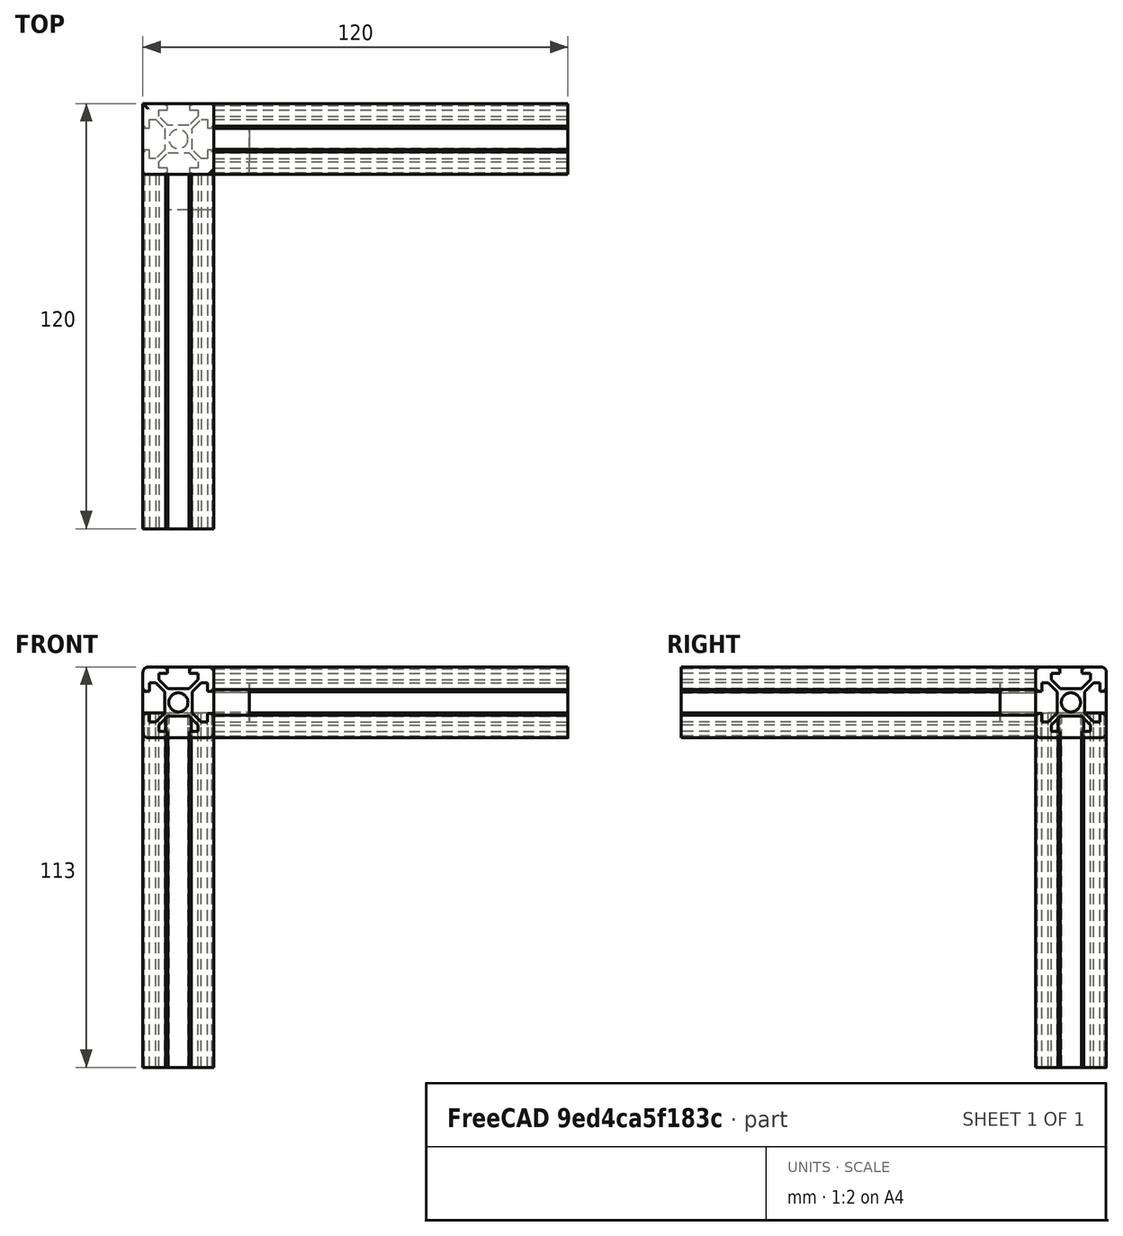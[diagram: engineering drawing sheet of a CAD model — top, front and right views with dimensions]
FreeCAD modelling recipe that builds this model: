
FCSTD DOCUMENT  (FreeCAD 1.0R39109 (Git))
Label: TopHatSpacer_removedinner
License: All rights reserved
LicenseURL: https://en.wikipedia.org/wiki/All_rights_reserved
objects: Part::FeaturePython×17, Part::Cut×8, Part::Feature×6, Part::Cylinder×6, Part::Plane×4, App::DocumentObjectGroup×4, Part::MultiFuse×3, Part::Box×2, PartDesign::FeatureBase×1, PartDesign::Fillet×1, PartDesign::Body×1
note: 52 computed .brp shape members not serialized (recipe doc carries the construction recipe); baked Part::Feature solids carry a one-line shape summary decoded from their .brp

FEATURE [Part::Feature] Part__Feature  label="Extrusion Profiles v3"
  shape: bbox 20 x 20 x 100 mm, 67 faces (baked)
FEATURE [Part::Cylinder] Cylinder
  Angle = 360
  AttacherType = Attacher::AttachEngine3D
  FirstAngle = 0
  Height = 100
  Placement = pos=(10,10,0) rot=(0,0,1;0rad)
  Radius = 2.7
  SecondAngle = 0
FEATURE [Part::Cut] Cut
  Base = -> Part__Feature
  Placement = pos=(0,5.68e-14,93) rot=(1,0,0;1.5708rad)
  Tool = -> Cylinder
FEATURE [Part::Cylinder] Cylinder001
  Angle = 360
  AttacherType = Attacher::AttachEngine3D
  FirstAngle = 0
  Height = 100
  Placement = pos=(10,10,0) rot=(0,0,1;0rad)
  Radius = 2.7
  SecondAngle = 0
FEATURE [Part::Feature] Part__Feature001  label="Extrusion Profiles v004"
  shape: bbox 20 x 20 x 100 mm, 67 faces (baked)
FEATURE [Part::Cut] Cut001
  Base = -> Part__Feature001
  Placement = pos=(20,0,113) rot=(0,1,0;1.5708rad)
  Tool = -> Cylinder001
FEATURE [Part::Cylinder] Cylinder002
  Angle = 360
  AttacherType = Attacher::AttachEngine3D
  FirstAngle = 0
  Height = 100
  Placement = pos=(10,10,0) rot=(0,0,1;0rad)
  Radius = 2.7
  SecondAngle = 0
FEATURE [Part::Feature] Part__Feature002  label="Extrusion Profiles v005"
  shape: bbox 20 x 20 x 100 mm, 67 faces (baked)
FEATURE [Part::Cut] Cut002
  Base = -> Part__Feature002
  Tool = -> Cylinder002
FEATURE [Part::Box] Box  label="Cube"
  AttacherType = Attacher::AttachEngine3D
  Height = 20
  Length = 30
  Placement = pos=(0,-10,93) rot=(0,0,1;0rad)
  Width = 30
FEATURE [Part::MultiFuse] Fusion
  Shapes = -> [Cut,Cut001,Cut002]
FEATURE [Part::Cut] Cut003
  Base = -> Box
  Tool = -> Fusion
FEATURE [Part::Box] Box001  label="Cube001"
  AttacherType = Attacher::AttachEngine3D
  Height = 30
  Length = 10
  Placement = pos=(20,-10,90) rot=(0,0,1;0rad)
  Width = 10
FEATURE [Part::Cut] Cut004
  Base = -> Cut003
  Tool = -> Box001
FEATURE [Part::Plane] Plane
  AttacherType = Attacher::AttachEngine3D
  Length = 100
  Placement = pos=(20,-40,157.445) rot=(0,1,0;1.5708rad)
  Width = 100
FEATURE [Part::FeaturePython] Slice  # WARN: FeaturePython — macro-defined, semantics opaque (R4)
  Base = -> Cut004
  Mode = 1
  Tolerance = 0
  Tools = -> [Plane]
FEATURE [Part::FeaturePython] Slice_child0  label="Slice.0"  # WARN: FeaturePython — macro-defined, semantics opaque (R4)
  Base = -> Slice
  FilterType = 1
  Invert = false
  OverrideMaxVal = 0
  WindowFrom = 80
  WindowTo = 100
  items = 0
FEATURE [App::DocumentObjectGroup] GrExplode_Slice  label="Exploded Slice"
  Group = -> [Slice_child0]
FEATURE [Part::FeaturePython] Slice_child6  label="Slice.6"  # WARN: FeaturePython — macro-defined, semantics opaque (R4)
  Base = -> Slice
  FilterType = 1
  Invert = false
  OverrideMaxVal = 0
  WindowFrom = 80
  WindowTo = 100
  items = 6
FEATURE [Part::FeaturePython] Slice_child8  label="Slice.8"  # WARN: FeaturePython — macro-defined, semantics opaque (R4)
  Base = -> Slice
  FilterType = 1
  Invert = false
  OverrideMaxVal = 0
  WindowFrom = 80
  WindowTo = 100
  items = 8
FEATURE [Part::Plane] Plane001
  AttacherType = Attacher::AttachEngine3D
  Length = 100
  Placement = pos=(-40,4.26e-14,57.4445) rot=(1,0,0;1.5708rad)
  Width = 100
FEATURE [Part::FeaturePython] Slice001  # WARN: FeaturePython — macro-defined, semantics opaque (R4)
  Base = -> Slice_child0
  Mode = 1
  Tolerance = 0
  Tools = -> [Plane001]
FEATURE [Part::FeaturePython] Slice001_child1  label="Slice001.1"  # WARN: FeaturePython — macro-defined, semantics opaque (R4)
  Base = -> Slice001
  FilterType = 1
  Invert = false
  OverrideMaxVal = 0
  WindowFrom = 80
  WindowTo = 100
  items = 1
FEATURE [App::DocumentObjectGroup] GrExplode_Slice001  label="Exploded Slice001"
  Group = -> [Slice001_child1]
FEATURE [Part::FeaturePython] Slice001_child6  label="Slice001.6"  # WARN: FeaturePython — macro-defined, semantics opaque (R4)
  Base = -> Slice001
  FilterType = 1
  Invert = false
  OverrideMaxVal = 0
  WindowFrom = 80
  WindowTo = 100
  items = 6
FEATURE [Part::FeaturePython] Slice001_child8  label="Slice001.8"  # WARN: FeaturePython — macro-defined, semantics opaque (R4)
  Base = -> Slice001
  FilterType = 1
  Invert = false
  OverrideMaxVal = 0
  WindowFrom = 80
  WindowTo = 100
  items = 8
FEATURE [Part::Plane] Plane002
  AttacherType = Attacher::AttachEngine3D
  Length = 100
  Placement = pos=(-40,-40,100) rot=(0,0,1;0rad)
  Width = 100
FEATURE [Part::FeaturePython] Slice002  # WARN: FeaturePython — macro-defined, semantics opaque (R4)
  Base = -> Slice001_child1
  Mode = 1
  Tolerance = 0
  Tools = -> [Plane002]
FEATURE [App::DocumentObjectGroup] GrExplode_Slice002  label="Exploded Slice002"
FEATURE [Part::FeaturePython] Slice002_child1  label="Slice002.1"  # WARN: FeaturePython — macro-defined, semantics opaque (R4)
  Base = -> Slice002
  FilterType = 1
  Invert = false
  OverrideMaxVal = 0
  WindowFrom = 80
  WindowTo = 100
  items = 1
FEATURE [Part::FeaturePython] Slice002_child3  label="Slice002.3"  # WARN: FeaturePython — macro-defined, semantics opaque (R4)
  Base = -> Slice002
  FilterType = 1
  Invert = false
  OverrideMaxVal = 0
  WindowFrom = 80
  WindowTo = 100
  items = 3
FEATURE [Part::FeaturePython] Slice002_child4  label="Slice002.4"  # WARN: FeaturePython — macro-defined, semantics opaque (R4)
  Base = -> Slice002
  FilterType = 1
  Invert = false
  OverrideMaxVal = 0
  WindowFrom = 80
  WindowTo = 100
  items = 4
FEATURE [Part::FeaturePython] Slice002_child5  label="Slice002.5"  # WARN: FeaturePython — macro-defined, semantics opaque (R4)
  Base = -> Slice002
  FilterType = 1
  Invert = false
  OverrideMaxVal = 0
  WindowFrom = 80
  WindowTo = 100
  items = 5
FEATURE [Part::FeaturePython] Slice002_child7  label="Slice002.7"  # WARN: FeaturePython — macro-defined, semantics opaque (R4)
  Base = -> Slice002
  FilterType = 1
  Invert = false
  OverrideMaxVal = 0
  WindowFrom = 80
  WindowTo = 100
  items = 7
FEATURE [Part::FeaturePython] Slice002_child9  label="Slice002.9"  # WARN: FeaturePython — macro-defined, semantics opaque (R4)
  Base = -> Slice002
  FilterType = 1
  Invert = false
  OverrideMaxVal = 0
  WindowFrom = 80
  WindowTo = 100
  items = 9
FEATURE [Part::MultiFuse] Fusion001
  Shapes = -> [Slice002_child9,Slice002_child7,Slice002_child5,Slice002_child4,Slice002_child3,Slice002_child1,Slice001_child8,Slice001_child6,Slice_child8,Slice_child6]
FEATURE [Part::Cylinder] Cylinder003
  Angle = 360
  AttacherType = Attacher::AttachEngine3D
  FirstAngle = 0
  Height = 100
  Placement = pos=(10,10,0) rot=(0,0,1;0rad)
  Radius = 2.7
  SecondAngle = 0
FEATURE [Part::Cylinder] Cylinder004
  Angle = 360
  AttacherType = Attacher::AttachEngine3D
  FirstAngle = 0
  Height = 100
  Placement = pos=(10,10,0) rot=(0,0,1;0rad)
  Radius = 2.7
  SecondAngle = 0
FEATURE [Part::Cylinder] Cylinder005
  Angle = 360
  AttacherType = Attacher::AttachEngine3D
  FirstAngle = 0
  Height = 100
  Placement = pos=(10,10,0) rot=(0,0,1;0rad)
  Radius = 2.7
  SecondAngle = 0
FEATURE [Part::Feature] Part__Feature003  label="Extrusion Profiles v006"
  shape: bbox 20 x 20 x 100 mm, 67 faces (baked)
FEATURE [Part::Cut] Cut005
  Base = -> Part__Feature003
  Placement = pos=(0,5.68e-14,93) rot=(1,0,0;1.5708rad)
  Tool = -> Cylinder003
FEATURE [Part::Feature] Part__Feature004  label="Extrusion Profiles v007"
  shape: bbox 20 x 20 x 100 mm, 67 faces (baked)
FEATURE [Part::Cut] Cut006
  Base = -> Part__Feature004
  Placement = pos=(20,0,113) rot=(0,1,0;1.5708rad)
  Tool = -> Cylinder004
FEATURE [Part::Feature] Part__Feature005  label="Extrusion Profiles v008"
  shape: bbox 20 x 20 x 100 mm, 67 faces (baked)
FEATURE [Part::Cut] Cut007
  Base = -> Part__Feature005
  Tool = -> Cylinder005
FEATURE [Part::MultiFuse] Fusion002
  Shapes = -> [Cut005,Cut006,Cut007]
FEATURE [PartDesign::FeatureBase] BaseFeature
  BaseFeature = -> Fusion001
  Suppressed = false
FEATURE [PartDesign::Fillet] Fillet
  Base = -> BaseFeature [Edge101,Edge91]
  BaseFeature = -> BaseFeature
  Radius = 1.5
  Refine = true
  SupportTransform = false
  Suppressed = false
  UseAllEdges = false
FEATURE [PartDesign::Body] Body
  AllowCompound = false
  BaseFeature = -> Fusion001
  Group = -> [BaseFeature,Fillet]
  Origin = -> Origin
  Tip = -> Fillet
FEATURE [Part::Plane] Plane003
  AttacherType = Attacher::AttachEngine3D
  Length = 10
  Placement = pos=(15.45,1.96,116.54) rot=(0.28,0.68,-0.68;1.09607rad)
  Width = 10
FEATURE [Part::FeaturePython] Slice003  # WARN: FeaturePython — macro-defined, semantics opaque (R4)
  Base = -> Fillet
  Mode = 1
  Tolerance = 0
  Tools = -> [Plane003]
FEATURE [Part::FeaturePython] Slice003_child0  label="Slice003.0"  # WARN: FeaturePython — macro-defined, semantics opaque (R4)
  Base = -> Slice003
  FilterType = 1
  Invert = false
  OverrideMaxVal = 0
  WindowFrom = 80
  WindowTo = 100
  items = 0
FEATURE [App::DocumentObjectGroup] GrExplode_Slice003  label="Exploded Slice003"
  Group = -> [Slice003_child0]
